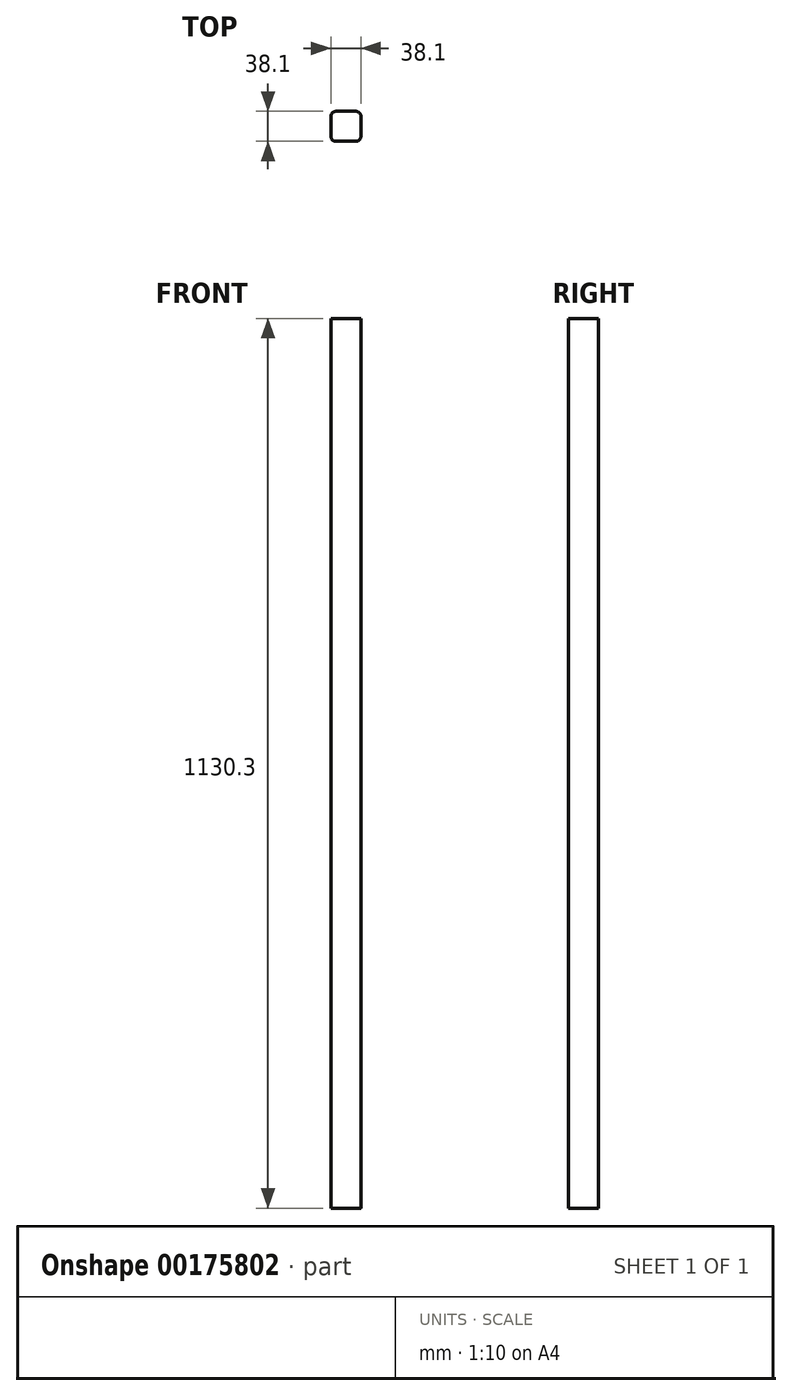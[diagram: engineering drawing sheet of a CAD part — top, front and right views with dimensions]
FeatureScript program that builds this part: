
annotation { "Feature Type Name" : "Feature", "Feature Type Description" : "" }
export const myFeature = defineFeature(function(context is Context, id is Id, definition is map)
    precondition{}
    {
        {
            var Q0;
            Q0=qCreatedBy(makeId("Top.planeOp"),FACE);
            var sketch = newSketch(context, id + "F0", { "sketchPlane" : qUnion([Q0])});
            skLineSegment(sketch, "E0.bottom", {"start": v(12.7, 19.05) * mm, "end": v(-12.7, 19.05) * mm});
            skLineSegment(sketch, "E0.top", {"start": v(12.7, -19.05) * mm, "end": v(-12.7, -19.05) * mm});
            skLineSegment(sketch, "E0.left", {"start": v(19.05, 12.7) * mm, "end": v(19.05, -12.7) * mm});
            skLineSegment(sketch, "E0.right", {"start": v(-19.05, 12.7) * mm, "end": v(-19.05, -12.7) * mm});
            skPoint(sketch, "E0.middle", {"position": v(0, 0) * mm});
            skPoint(sketch, "E1.visualSharp", {"position": v(-19.05, 19.05) * mm});
            skArc(sketch, "E1.filletArc", {"start": v(-12.7, 19.05) * mm, "mid": v(-17.2, 17.2) * mm, "end": v(-19.05, 12.7) * mm});
            skPoint(sketch, "E2.visualSharp", {"position": v(19.05, 19.05) * mm});
            skArc(sketch, "E2.filletArc", {"start": v(19.05, 12.7) * mm, "mid": v(17.2, 17.2) * mm, "end": v(12.7, 19.05) * mm});
            skPoint(sketch, "E3.visualSharp", {"position": v(19.05, -19.05) * mm});
            skArc(sketch, "E3.filletArc", {"start": v(12.7, -19.05) * mm, "mid": v(17.2, -17.2) * mm, "end": v(19.05, -12.7) * mm});
            skPoint(sketch, "E4.visualSharp", {"position": v(-19.05, -19.05) * mm});
            skArc(sketch, "E4.filletArc", {"start": v(-19.05, -12.7) * mm, "mid": v(-17.2, -17.2) * mm, "end": v(-12.7, -19.05) * mm});
            skSolve(sketch);
        }
        {
            var Q0;
            Q0=qSketchRegion(id+"F0",true);
            extrude(context, id + "F1", {"entities" : qUnion([Q0]), "depth" : 1130.3 * mm, "offsetDistance" : 25.4 * mm});
        }
    });
